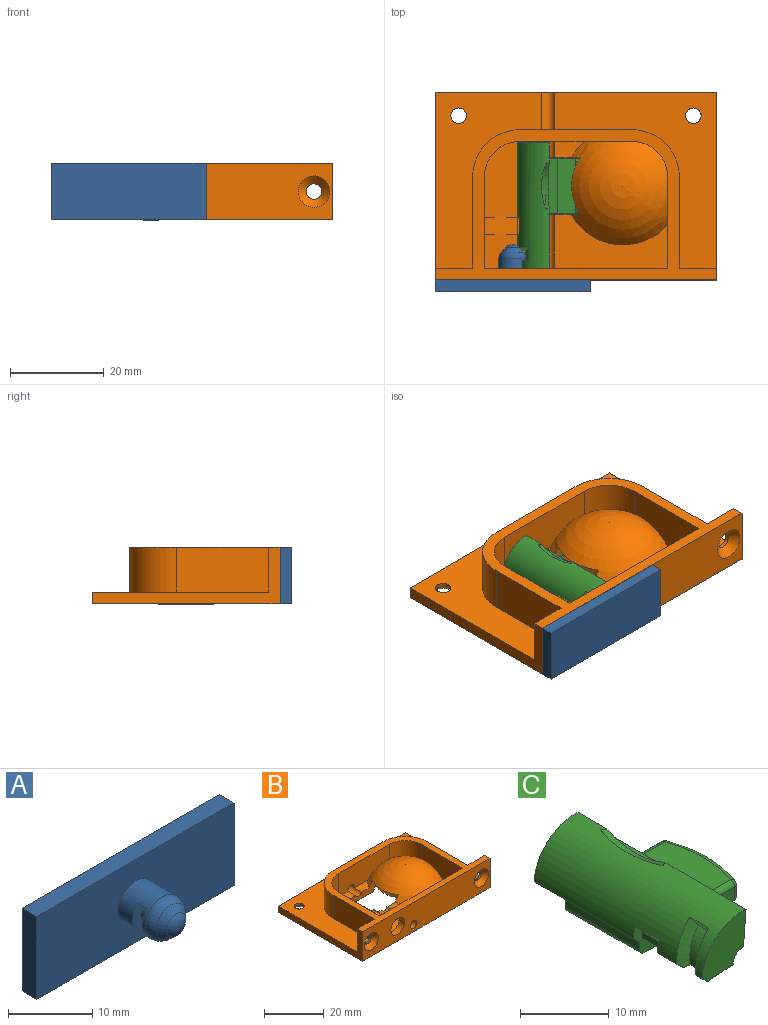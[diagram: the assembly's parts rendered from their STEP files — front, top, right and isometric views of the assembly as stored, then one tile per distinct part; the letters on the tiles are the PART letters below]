
ASSEMBLY  parts=3 mates=2
PART A: 16 faces, bbox 33x10x12 mm
  f0: plane 5.04x2.95mm, normal (0,1,0), area 7.2mm2, adj f8,f9,f14,f15
  f1: plane 12x2.5mm, normal (1,0,0), area 30mm2, adj f2,f4,f5,f6
  f2: plane 33x2.5mm, normal (0,0,1), area 82.5mm2, adj f1,f3,f5,f6
  f3: plane 12x2.5mm, normal (-1,0,0), area 30mm2, adj f2,f4,f5,f6
  f4: plane 33x2.5mm, normal (0,0,-1), area 82.5mm2, adj f1,f3,f5,f6
  f5: plane 33x12mm, normal (0,1,0), area 396mm2, adj f1,f2,f3,f4
  f6: plane 33x12mm, normal (0,-1,0), area 368.7mm2, adj f1,f2,f3,f4,f9
  f7: plane 5.04x2.95mm, normal (0,-1,0), area 7.2mm2, adj f8,f9,f14,f15
  f8: cylinder r=1.6mm len=2.73mm, axis (0,1,0), area 6mm2, adj f0,f7,f14,f15
  f9: cylinder r=2.95mm len=5.9mm, axis (0,1,0), area 73.8mm2, adj f0,f6,f7,f12,f14,f15
  f10: cone r=2.95mm half-angle=42.2deg, axis (0,1,0), area 15.7mm2, adj f12,f13
  f11: plane 0.23x0.23mm, normal (0,-1,0), area 0mm2, adj f13
  f12: torus R=0.95mm, axis (0,-1,0), area 25.7mm2, adj f9,f10
  f13: torus R=0.11mm, axis (0,1,0), area 9.4mm2, adj f10,f11
  f14: plane 1.6x0.95mm, normal (-0.71,0,-0.71), area 2.2mm2, adj f0,f7,f8,f9
  f15: plane 1.6x1.35mm, normal (-1,0,0), area 2.2mm2, adj f0,f7,f8,f9
PART B: 50 faces, bbox 60.1x40.1x12.1 mm
  f0: plane 9.5x8.6mm, normal (1,0,0), area 81.7mm2, adj f1,f9,f35,f37
  f1: plane 27x12.09mm, normal (0,0,1), area 232.3mm2, adj f0,f18,f20,f21,f24,f25,f26,f27
  f2: plane 60x2.5mm, normal (0,1,0), area 147.9mm2, adj f3,f4,f7,f8,f11,f27
  f3: plane 37.5x34.59mm, normal (0,0,1), area 525.6mm2, adj f2,f8,f12,f13,f16,f27,f39,f44
  f4: plane 37.5x22.59mm, normal (0,0,1), area 429.6mm2, adj f2,f7,f14,f15,f16,f27,f38,f42
  f5: plane 6.42x3.5mm, normal (0,0,1), area 16.9mm2, adj f18,f22,f24,f27
  f6: plane 24.09x11.5mm, normal (0,0,1), area 176.5mm2, adj f19,f20,f22,f25,f26
  f7: plane 40x12mm, normal (-1,0,0), area 123.8mm2, adj f2,f4,f9,f10,f11,f14
  f8: plane 40x12mm, normal (1,0,0), area 123.8mm2, adj f2,f3,f9,f10,f11,f13
  f9: plane 60x32mm, normal (0,0,1), area 376.2mm2, adj f0,f7,f8,f10,f12,f13,f14,f15
  f10: plane 60x12mm, normal (0,-1,0), area 608.8mm2, adj f7,f8,f9,f11,f26,f28,f47,f49
  f11: plane 60x40mm, normal (0,0,-1), area 1796.1mm2, adj f2,f7,f8,f10,f24,f25,f29,f41
  f12: plane 19.5x9.5mm, normal (1,0,0), area 185.2mm2, adj f3,f9,f13,f39
  f13: plane 9.5x8mm, normal (0,1,0), area 67.4mm2, adj f3,f8,f9,f12,f46
  f14: plane 9.5x8mm, normal (0,1,0), area 67.4mm2, adj f4,f7,f9,f15,f48
  f15: plane 19.5x9.5mm, normal (-1,0,0), area 185.2mm2, adj f4,f9,f14,f38
  f16: plane 24x9.5mm, normal (0,1,0), area 223mm2, adj f3,f4,f9,f27,f38,f39
  f17: sphere r=12mm, area 474.7mm2, adj f23,f24,f25,f41
  f18: plane 24x9.5mm, normal (0,-1,0), area 195.1mm2, adj f1,f5,f9,f22,f27,f36,f37
  f19: plane 19.5x9.5mm, normal (-1,0,0), area 157.4mm2, adj f6,f9,f20,f22,f36
  f20: plane 39x9.5mm, normal (0,1,0), area 332.3mm2, adj f1,f6,f9,f19,f21,f26,f28
  f21: plane 9.5x7.1mm, normal (1,0,0), area 67.4mm2, adj f1,f9,f20,f34
  f22: sphere r=14.5mm, area 492.4mm2, adj f5,f6,f18,f19,f24,f25,f36,f40
  f23: plane 12x3.11mm, normal (0,0,-1), area 11.5mm2, adj f17,f24,f25,f40
  f24: plane 14.88x4.79mm, normal (0,-1,0), area 34.6mm2, adj f1,f5,f11,f17,f22,f23,f27,f29
  f25: plane 14.88x4.79mm, normal (0,1,0), area 34.6mm2, adj f1,f6,f11,f17,f22,f23,f26,f29
  f26: cylinder r=1.5mm len=14mm, axis (0,1,0), area 66mm2, adj f1,f6,f10,f20,f25
  f27: cylinder r=1.5mm len=14mm, axis (0,1,0), area 66mm2, adj f1,f2,f3,f4,f5,f16,f18,f24
  f28: cylinder r=3.25mm len=6.5mm, axis (0,-1,0), area 51.1mm2, adj f10,f20
  f29: cylinder r=5.83mm len=12mm, axis (0,-1,0), area 31.8mm2, adj f1,f11,f24,f25
  f30: cylinder r=5.83mm len=3.8mm, axis (0,1,0), area 4mm2, adj f1,f31,f34,f35
  f31: cylinder r=0.75mm len=3.8mm, axis (0,1,0), area 10mm2, adj f30,f32,f34,f35
  f32: plane 3.8x0.97mm, normal (0,0,1), area 3.7mm2, adj f31,f33,f34,f35
  f33: plane 7x7mm, normal (0.71,0,0.71), area 37.6mm2, adj f9,f32,f34,f35
  f34: plane 9.5x8.72mm, normal (0,-1,0), area 45mm2, adj f1,f21,f30,f31,f32,f33
  f35: plane 9.5x8.72mm, normal (0,1,0), area 45mm2, adj f0,f1,f30,f31,f32,f33
  f36: cylinder r=7.5mm len=7.5mm, axis (0,0,-1), area 75.6mm2, adj f9,f18,f19,f22
  f37: cylinder r=7.5mm len=9.5mm, axis (0,0,1), area 111.9mm2, adj f0,f1,f9,f18
  f38: cylinder r=10mm len=10mm, axis (0,0,-1), area 149.2mm2, adj f4,f9,f15,f16
  f39: cylinder r=10mm len=10mm, axis (0,0,1), area 149.2mm2, adj f3,f9,f12,f16
  f40: cone r=10.93mm half-angle=24.4deg, axis (0,0,1), area 25.8mm2, adj f22,f23,f24,f25
  f41: torus R=11.45mm, axis (0,0,1), area 44.9mm2, adj f11,f17,f24,f25
  f42: cylinder r=1.65mm len=3.3mm, axis (0,0,-1), area 8.2mm2, adj f4,f43
  f43: cone r=1.65mm half-angle=45deg, axis (0,0,-1), area 38.1mm2, adj f11,f42
  f44: cylinder r=1.65mm len=3.3mm, axis (0,0,-1), area 8.2mm2, adj f3,f45
  f45: cone r=1.65mm half-angle=45deg, axis (0,0,-1), area 38.1mm2, adj f11,f44
  f46: cylinder r=1.65mm len=3.3mm, axis (0,-1,0), area 8.2mm2, adj f13,f47
  f47: cone r=1.65mm half-angle=45deg, axis (0,-1,0), area 38.1mm2, adj f10,f46
  f48: cylinder r=1.65mm len=3.3mm, axis (0,-1,0), area 8.2mm2, adj f14,f49
  f49: cone r=1.65mm half-angle=45deg, axis (0,-1,0), area 38.1mm2, adj f10,f48
PART C: 43 faces, bbox 20.2x26.8x10.5 mm
  f0: plane 26.7x4.98mm, normal (1,0,-0.08), area 96.7mm2, adj f1,f5,f7,f9,f11,f12,f20,f37
  f1: cylinder r=6.5mm len=26.7mm, axis (0,-1,0), area 239.4mm2, adj f0,f2,f11,f12,f14,f15,f16,f17
  f2: plane 3.37x0.93mm, normal (-0.7,0,-0.71), area 3.8mm2, adj f1,f10,f14,f31
  f3: plane 10.4x5.46mm, normal (0,0,1), area 53.6mm2, adj f19,f21,f23,f24
  f4: plane 11.8x1.93mm, normal (-1,0,0), area 22.8mm2, adj f5,f7,f10,f29
  f5: plane 15.13x7.09mm, normal (0,-1,0), area 49.1mm2, adj f0,f4,f8,f9,f10,f19,f20,f23
  f6: cylinder r=15.55mm len=10.89mm, axis (0,0,-1), area 12.2mm2, adj f24,f25,f27,f28
  f7: plane 15.13x7.09mm, normal (0,1,0), area 49.1mm2, adj f0,f4,f8,f9,f10,f19,f20,f21
  f8: plane 15.36x11.8mm, normal (0,0,-1), area 176.6mm2, adj f5,f7,f27,f29
  f9: cylinder r=1.5mm len=26.7mm, axis (0,1,0), area 149.4mm2, adj f0,f5,f7,f10,f11,f12,f35
  f10: plane 25.8x4.13mm, normal (0.08,0,-1), area 62.3mm2, adj f2,f4,f5,f7,f9,f12,f13,f14
  f11: plane 7.01x6.1mm, normal (0,1,0), area 30mm2, adj f0,f1,f9,f17,f35
  f12: plane 7.01x6.93mm, normal (0,-1,0), area 34.2mm2, adj f0,f1,f9,f10,f18
  f13: cylinder r=4.7mm len=4.16mm, axis (0,-1,0), area 11.3mm2, adj f10,f14,f15,f16
  f14: bspline ~5.94x4.09mm, area 10.1mm2, adj f1,f2,f10,f13,f16
  f15: bspline ~5.94x4.09mm, area 10.1mm2, adj f1,f10,f13,f16,f18
  f16: plane 3x1.46mm, normal (-0.81,0,-0.59), area 4.8mm2, adj f1,f13,f14,f15
  f17: plane 15.8x0.86mm, normal (-0.7,0,-0.71), area 18.6mm2, adj f1,f10,f11,f32,f35
  f18: plane 1.17x0.93mm, normal (-0.7,0,-0.71), area 1.3mm2, adj f1,f10,f12,f15
  f19: plane 11.8x5.29mm, normal (0.8,0,0.6), area 68.2mm2, adj f3,f5,f7,f20,f21,f23
  f20: plane 11.8x2mm, normal (0,0,1), area 23.6mm2, adj f0,f5,f7,f19
  f21: cylinder r=0.7mm len=4.52mm, axis (1,0,0), area 4.8mm2, adj f3,f7,f19,f22
  f22: sphere r=0.7mm, area 0.6mm2, adj f21,f24,f25
  f23: cylinder r=0.7mm len=4.52mm, axis (-1,0,0), area 4.8mm2, adj f3,f5,f19,f26
  f24: torus R=14.85mm, axis (0,0,1), area 12mm2, adj f3,f6,f22,f26
  f25: cylinder r=0.7mm len=1.75mm, axis (0,0,-1), area 1.2mm2, adj f6,f7,f22,f27
  f26: sphere r=0.7mm, area 0.6mm2, adj f23,f24,f28
  f27: torus R=14.85mm, axis (0,0,1), area 13mm2, adj f5,f6,f7,f8,f25,f28
  f28: cylinder r=0.7mm len=1.75mm, axis (0,0,-1), area 1.2mm2, adj f5,f6,f26,f27
  f29: cylinder r=0.7mm len=11.8mm, axis (0,-1,0), area 13mm2, adj f4,f5,f7,f8
  f30: plane 3.8x0.65mm, normal (-0.01,0,-1), area 2.5mm2, adj f1,f31,f32,f34
  f31: plane 2.47x1.71mm, normal (0,1,0), area 3.1mm2, adj f1,f2,f10,f30,f33,f34,f36
  f32: plane 2.47x1.71mm, normal (0,-1,0), area 3.1mm2, adj f1,f10,f17,f30,f33,f34,f36
  f33: cylinder r=5.13mm len=3.8mm, axis (0,1,0), area 2.9mm2, adj f31,f32,f34,f36
  f34: cylinder r=0.75mm len=3.8mm, axis (0,1,0), area 7.2mm2, adj f30,f31,f32,f33
  f35: plane 5.26x1.29mm, normal (0.05,0.71,-0.71), area 5.9mm2, adj f9,f10,f11,f17
  f36: plane 3.8x0.32mm, normal (-0.67,0,-0.74), area 1.7mm2, adj f10,f31,f32,f33
  f37: cone r=10.93mm half-angle=24.4deg, axis (-0.97,0,0.25), area 8mm2, adj f0,f1,f38
  f38: sphere r=14.5mm, area 8.6mm2, adj f1,f37
  f39: plane 0.19x0.13mm, normal (0,-1,0), area 0mm2, adj f0,f1,f40
  f40: sphere r=14.5mm, area 0mm2, adj f0,f1,f39
  f41: sphere r=14.5mm, area 0mm2, adj f0,f1,f42
  f42: plane 0.19x0.13mm, normal (0,1,0), area 0mm2, adj f0,f1,f41
PLACE A rot(axis=(0,0,1),180deg) t=(33,-80,0)mm
PLACE B at identity fixed
PLACE C rot(axis=(0,-1,0),2.3deg) t=(0.14,0,-0.97)mm
MATE revolute B.f26 <-> C.f1  axis (0,-1,0) through (24,-20,3)mm
MATE fastened B.f28 <-> A.f8  axis (0,-1,0) through (16.5,-40,6)mm
